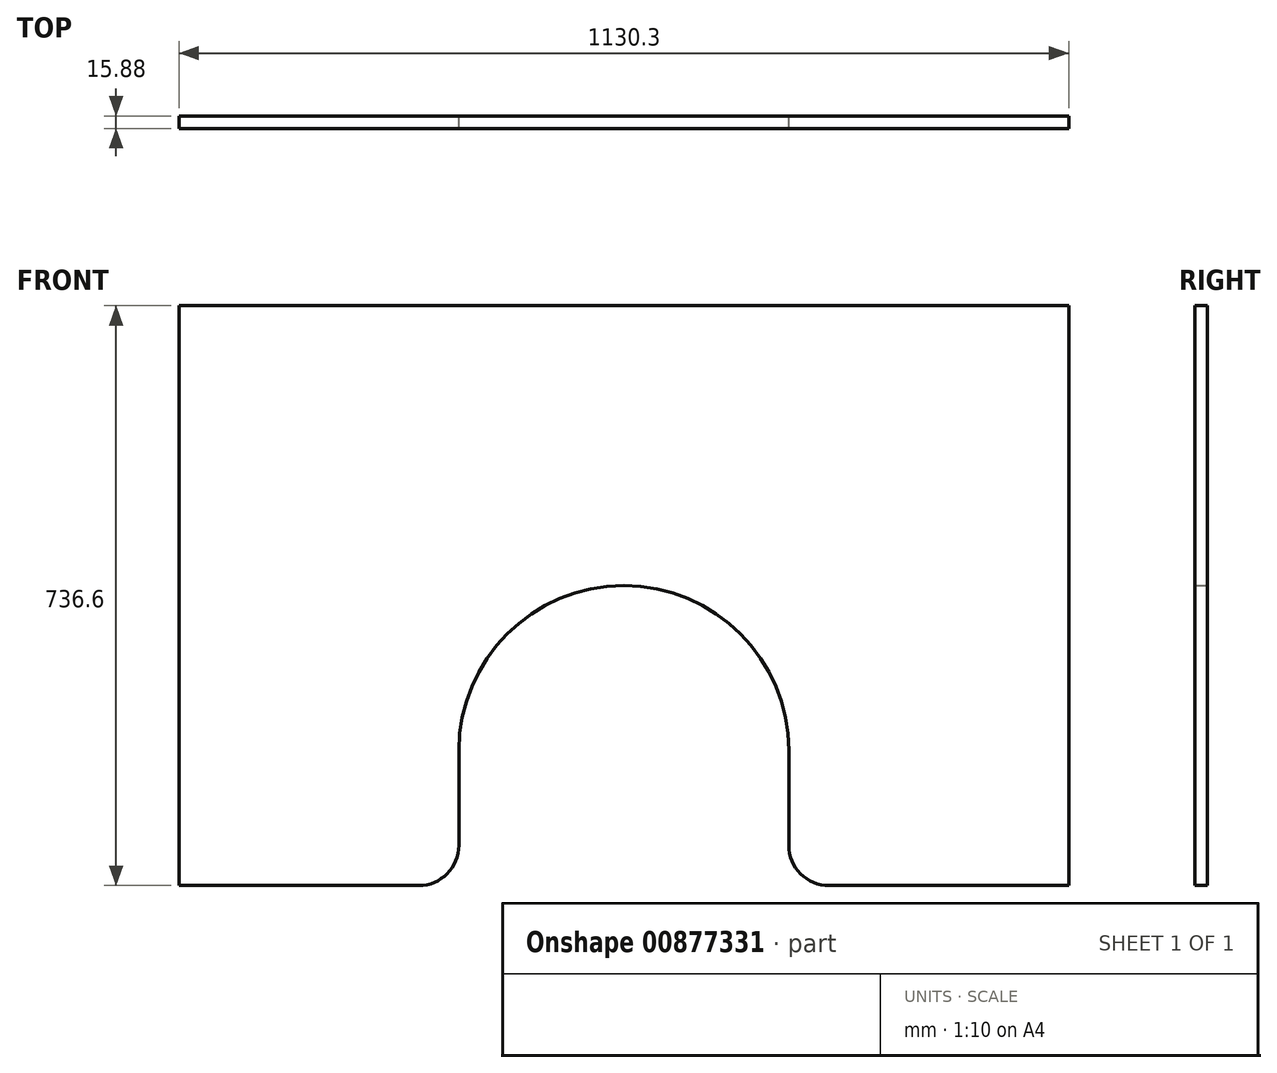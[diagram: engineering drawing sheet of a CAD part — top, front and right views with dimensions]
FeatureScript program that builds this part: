
annotation { "Feature Type Name" : "Feature", "Feature Type Description" : "" }
export const myFeature = defineFeature(function(context is Context, id is Id, definition is map)
    precondition{}
    {
        {
            var Q0;
            Q0=qCreatedBy(makeId("Front.planeOp"),FACE);
            var sketch = newSketch(context, id + "F0", { "sketchPlane" : qUnion([Q0])});
            skLineSegment(sketch, "E0", {"start": v(-70.81, 522.48) * mm, "end": v(1059.49, 522.48) * mm});
            skLineSegment(sketch, "E1", {"start": v(1059.49, 522.48) * mm, "end": v(1059.49, -214.12) * mm});
            skLineSegment(sketch, "E2", {"start": v(-70.81, 522.48) * mm, "end": v(-70.81, -214.12) * mm});
            skLineSegment(sketch, "E3", {"start": v(-70.81, -214.12) * mm, "end": v(233.99, -214.12) * mm});
            skLineSegment(sketch, "E4", {"start": v(1059.49, -214.12) * mm, "end": v(754.69, -214.12) * mm});
            skPoint(sketch, "E5.start.orphan", {"position": v(494.34, 522.48) * mm});
            skArc(sketch, "E6", {"start": v(703.89, -42.67) * mm, "mid": v(494.34, 166.88) * mm, "end": v(284.79, -42.67) * mm});
            skLineSegment(sketch, "E7", {"start": v(703.89, -163.32) * mm, "end": v(703.89, -42.67) * mm});
            skLineSegment(sketch, "E8", {"start": v(284.79, -163.32) * mm, "end": v(284.79, -42.67) * mm});
            skArc(sketch, "E9", {"start": v(233.99, -214.12) * mm, "mid": v(269.9, -199.24) * mm, "end": v(284.79, -163.32) * mm});
            skArc(sketch, "E10", {"start": v(703.89, -163.32) * mm, "mid": v(718.76, -199.24) * mm, "end": v(754.69, -214.12) * mm});
            skSolve(sketch);
        }
        {
            var Q0;
            Q0 = qSketchRegion(id + "F0", true);
            extrude(context, id + "F1", {"entities" : qUnion([Q0]), "depth" : 15.88 * mm, "offsetDistance" : 25.4 * mm});
        }
    });
